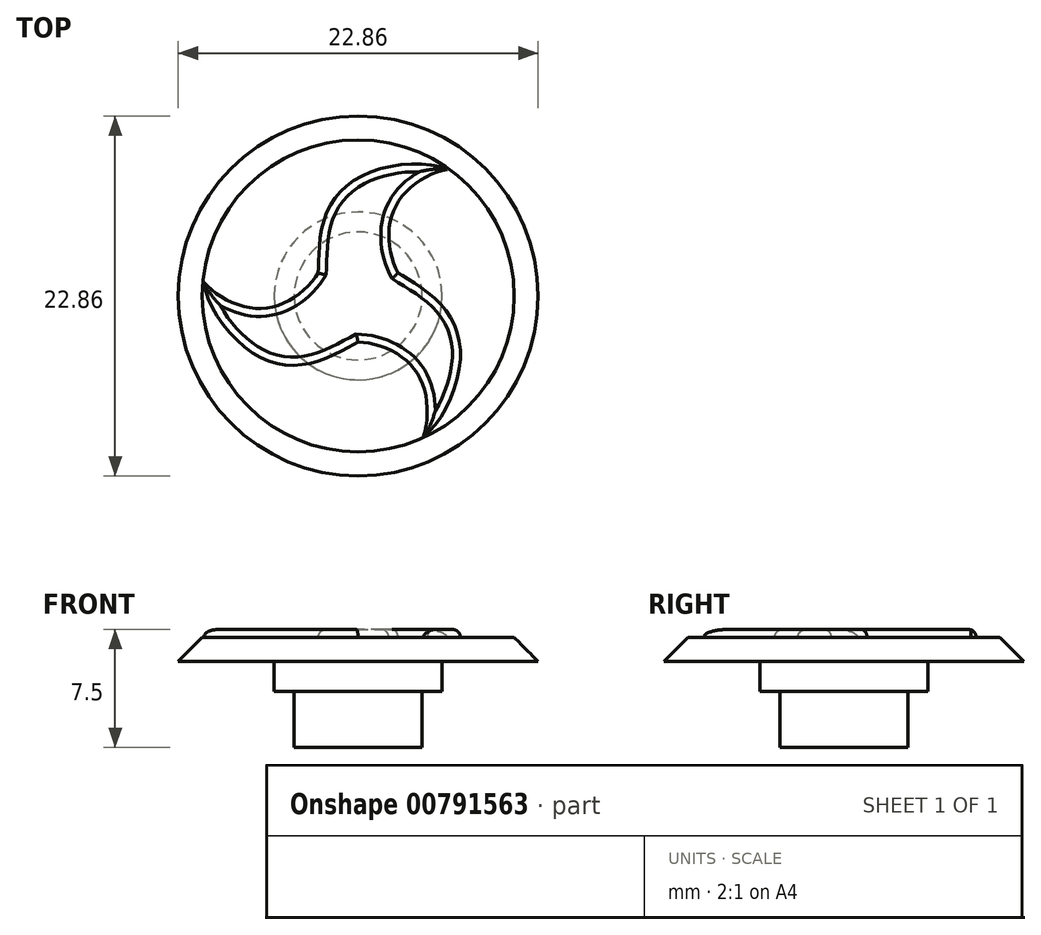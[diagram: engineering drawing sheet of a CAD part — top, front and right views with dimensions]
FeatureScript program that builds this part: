
annotation { "Feature Type Name" : "Feature", "Feature Type Description" : "" }
export const myFeature = defineFeature(function(context is Context, id is Id, definition is map)
    precondition{}
    {
        {
            var Q0;
            Q0=qCreatedBy(makeId("Top.planeOp"),FACE);
            var sketch = newSketch(context, id + "F0", { "sketchPlane" : qUnion([Q0])});
            skCircle(sketch, "E0", {"center": v(0, 0) * mm, "radius": 4.06 * mm});
            skSolve(sketch);
        }
        {
            var Q0;
            Q0 = qSketchRegion(id + "F0", true);
            extrude(context, id + "F1", {"entities" : qUnion([Q0]), "depth" : 4.32 * mm, "offsetDistance" : 25.4 * mm, "hasSecondDirection" : true, "secondDirectionOppositeDirection" : true, "secondDirectionDepth" : 1.9 * mm});
        }
        {
            var Q0;
            Q0=qCreatedBy(makeId("Top.planeOp"),FACE);
            var sketch = newSketch(context, id + "F2", { "sketchPlane" : qUnion([Q0])});
            skCircle(sketch, "E1", {"center": v(0, 0) * mm, "radius": 11.43 * mm});
            skSolve(sketch);
        }
        {
            var Q0;
            Q0 = qSketchRegion(id + "F2", true);
            extrude(context, id + "F3", {"entities" : qUnion([Q0]), "operationType" : NewBodyOperationType.ADD, "depth" : 5.08 * mm, "offsetDistance" : 25.4 * mm, "hasSecondDirection" : true, "secondDirectionOppositeDirection" : false, "secondDirectionDepth" : 3.56 * mm});
        }
        {
            var Q0;
            Q0=makeQuery(id+"F3.opExtrude","CAP_FACE",FACE,{"disambiguationData":[OSD([sQuery(id+"F2.wireOp",EDGE,"E1")])],"isStart":false});
            var sketch = newSketch(context, id + "F4", { "sketchPlane" : qUnion([Q0])});
            skLineSegment(sketch, "E2", {"start": v(0, 16.08) * mm, "end": v(0, -18.78) * mm, "construction": true});
            skFitSpline(sketch, "E3.MirrorCS", {"points": [v(-2.54, 1.47) * mm, v(-2.21, 4.66) * mm, v(0.44, 7.72) * mm, v(5.64, 8.04) * mm], "startDerivative": vector(0.42, 6.66) * mm, "endDerivative": vector(10.01, -4.69) * mm});
            skFitSpline(sketch, "E4.MirrorCS", {"points": [v(5.64, 8.04) * mm, v(3.1, 6.68) * mm, v(1.96, 4.21) * mm, v(2.54, 1.47) * mm], "startDerivative": vector(-6.98, -1.07) * mm, "endDerivative": vector(3.76, -6.3) * mm});
            skFitSpline(sketch, "E5.MirrorCS", {"points": [v(-9.79, 0.87) * mm, v(-7.33, -0.65) * mm, v(-4.63, -0.4) * mm, v(-2.54, 1.47) * mm], "startDerivative": vector(4.42, -5.5) * mm, "endDerivative": vector(3.58, 6.41) * mm});
            skFitSpline(sketch, "E6.MirrorCS", {"points": [v(0, -2.93) * mm, v(-2.93, -4.25) * mm, v(-6.9, -3.48) * mm, v(-9.79, 0.87) * mm], "startDerivative": vector(-5.98, -2.97) * mm, "endDerivative": vector(-0.94, 11.01) * mm});
            skFitSpline(sketch, "E7.MirrorCS", {"points": [v(4.14, -8.9) * mm, v(4.23, -6.03) * mm, v(2.67, -3.8) * mm, v(0, -2.93) * mm], "startDerivative": vector(2.56, 6.58) * mm, "endDerivative": vector(-7.34, -0.1) * mm});
            skFitSpline(sketch, "E8.MirrorCS", {"points": [v(2.54, 1.47) * mm, v(5.14, -0.41) * mm, v(6.47, -4.24) * mm, v(4.14, -8.9) * mm], "startDerivative": vector(5.56, -3.7) * mm, "endDerivative": vector(-9.07, -6.33) * mm});
            skSolve(sketch);
        }
        {
            var Q0;
            Q0=makeQuery(id+"F4.imprint","IMPRINT",FACE,{"disambiguationData":[TD([[makeQuery(id+"F4.imprint","IMPRINT",EDGE,{"derivedFrom":sQuery(id+"F4.wireOp",EDGE,"E3.MirrorCS")}),-1.0]])]});
            extrude(context, id + "F5", {"entities" : qUnion([Q0]), "operationType" : NewBodyOperationType.ADD, "depth" : 0.5 * mm, "offsetDistance" : 25.4 * mm});
        }
        {
            var Q0;
            Q0=makeQuery(id+"F5.opExtrude","CAP_EDGE",EDGE,{"disambiguationData":[OSD([sQuery(id+"F4.wireOp",EDGE,"E3.MirrorCS")])],"isStart":false});
            var Q1;
            Q1=makeQuery(id+"F5.opExtrude","CAP_EDGE",EDGE,{"disambiguationData":[OSD([sQuery(id+"F4.wireOp",EDGE,"E4.MirrorCS")])],"isStart":false});
            var Q2;
            Q2=makeQuery(id+"F5.opExtrude","CAP_EDGE",EDGE,{"disambiguationData":[OSD([sQuery(id+"F4.wireOp",EDGE,"E8.MirrorCS")])],"isStart":false});
            var Q3;
            Q3=makeQuery(id+"F5.opExtrude","CAP_EDGE",EDGE,{"disambiguationData":[OSD([sQuery(id+"F4.wireOp",EDGE,"E7.MirrorCS")])],"isStart":false});
            var Q4;
            Q4=makeQuery(id+"F5.opExtrude","CAP_EDGE",EDGE,{"disambiguationData":[OSD([sQuery(id+"F4.wireOp",EDGE,"E6.MirrorCS")])],"isStart":false});
            var Q5;
            Q5=makeQuery(id+"F5.opExtrude","CAP_EDGE",EDGE,{"disambiguationData":[OSD([sQuery(id+"F4.wireOp",EDGE,"E5.MirrorCS")])],"isStart":false});
            fillet(context, id + "F6", {"entities" : qUnion([Q0, Q1, Q2, Q3, Q4, Q5]), "radius" : 0.5 * mm, "tangentPropagation" : true, "allowEdgeOverflow" : false});
        }
        {
            var Q0;
            Q0=makeQuery(id+"F3.opExtrude","CAP_EDGE",EDGE,{"disambiguationData":[OSD([sQuery(id+"F2.wireOp",EDGE,"E1")])],"isStart":false});
            chamfer(context, id + "F7", {"entities" : qUnion([Q0]), "width" : 1.52 * mm, "tangentPropagation" : true});
        }
        {
            var Q0;
            Q0=makeQuery(id+"F3.opExtrude","CAP_FACE",FACE,{"disambiguationData":[OSD([sQuery(id+"F2.wireOp",EDGE,"E1")])],"isStart":true});
            var sketch = newSketch(context, id + "F8", { "sketchPlane" : qUnion([Q0])});
            skCircle(sketch, "E9", {"center": v(0, 0) * mm, "radius": 5.33 * mm});
            skSolve(sketch);
        }
        {
            var Q0;
            Q0=makeQuery(id+"F8.imprint","IMPRINT",FACE,{"disambiguationData":[TD([[makeQuery(id+"F8.imprint","IMPRINT",EDGE,{"derivedFrom":sQuery(id+"F8.wireOp",EDGE,"E9")}),1.0]])]});
            extrude(context, id + "F9", {"entities" : qUnion([Q0]), "operationType" : NewBodyOperationType.ADD, "depth" : 1.9 * mm, "offsetDistance" : 25.4 * mm});
        }
    });
